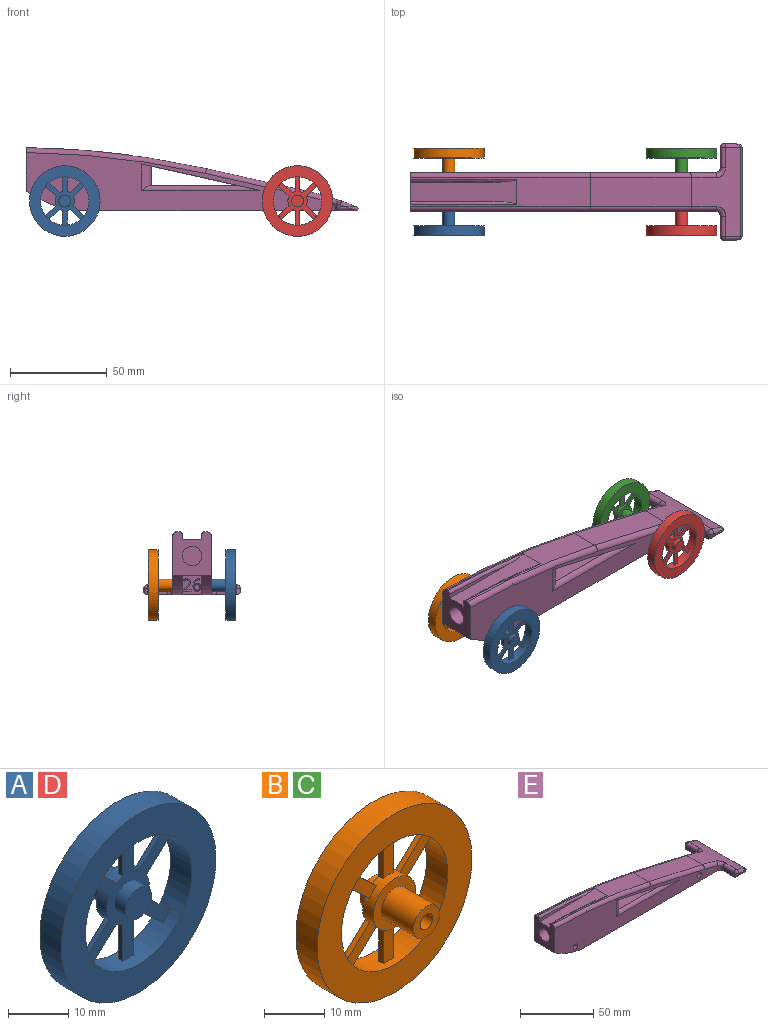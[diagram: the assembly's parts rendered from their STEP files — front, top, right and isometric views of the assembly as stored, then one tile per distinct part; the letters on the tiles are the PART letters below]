
ASSEMBLY  parts=5 mates=4
PART A: 31 faces, bbox 36.4x12.5x36.4 mm
  f0: cylinder r=3.1mm len=7.5mm, axis (0,1,0), area 146.1mm2, adj f2,f5
  f1: cylinder r=1.5mm len=10mm, axis (0,1,0), area 94.2mm2, adj f2,f3
  f2: plane 6.2x6.2mm, normal (0,1,0), area 23.1mm2, adj f0,f1
  f3: plane 3x3mm, normal (0,1,0), area 7.1mm2, adj f1
  f4: cylinder r=5mm len=10mm, axis (0,-1,0), area 64mm2, adj f5,f6,f9,f10,f11,f12,f13,f14
  f5: plane 10x10mm, normal (0,1,0), area 48.3mm2, adj f0,f4
  f6: plane 25.02x19.87mm, normal (0,-1,0), area 156.8mm2, adj f4,f8,f9,f10,f12,f13,f15,f16
  f7: plane 6.18x6.18mm, normal (0,-1,0), area 30mm2, adj f8
  f8: cylinder r=3.09mm len=6.18mm, axis (0,1,0), area 48.5mm2, adj f6,f7
  f9: plane 5.55x5.17mm, normal (0.68,0,-0.73), area 7.6mm2, adj f4,f6,f11,f27
  f10: plane 5.55x5.17mm, normal (-0.68,0,0.73), area 7.6mm2, adj f4,f6,f11,f27
  f11: plane 7.19x6.93mm, normal (0,1,0), area 18.1mm2, adj f4,f9,f10,f27
  f12: plane 7.59x1mm, normal (1,0,0), area 7.6mm2, adj f4,f6,f14,f27
  f13: plane 7.59x1mm, normal (-1,0,0), area 7.6mm2, adj f4,f6,f14,f27
  f14: plane 7.65x2.4mm, normal (0,1,0), area 18.1mm2, adj f4,f12,f13,f27
  f15: plane 5.55x5.17mm, normal (-0.68,0,-0.73), area 7.6mm2, adj f4,f6,f17,f27
  f16: plane 5.55x5.17mm, normal (0.68,0,0.73), area 7.6mm2, adj f4,f6,f17,f27
  f17: plane 7.19x6.93mm, normal (0,1,0), area 18.1mm2, adj f4,f15,f16,f27
  f18: plane 5.55x5.17mm, normal (-0.68,0,0.73), area 7.6mm2, adj f4,f6,f20,f27
  f19: plane 5.55x5.17mm, normal (0.68,0,-0.73), area 7.6mm2, adj f4,f6,f20,f27
  f20: plane 7.19x6.93mm, normal (0,1,0), area 18.1mm2, adj f4,f18,f19,f27
  f21: plane 7.59x1mm, normal (-1,0,0), area 7.6mm2, adj f4,f6,f23,f27
  f22: plane 7.59x1mm, normal (1,0,0), area 7.6mm2, adj f4,f6,f23,f27
  f23: plane 7.65x2.4mm, normal (0,1,0), area 18.1mm2, adj f4,f21,f22,f27
  f24: plane 5.55x5.17mm, normal (-0.68,0,-0.73), area 7.6mm2, adj f4,f6,f26,f27
  f25: plane 5.55x5.17mm, normal (0.68,0,0.73), area 7.6mm2, adj f4,f6,f26,f27
  f26: plane 7.19x6.93mm, normal (0,1,0), area 18.1mm2, adj f4,f24,f25,f27
  f27: cylinder r=12.5mm len=25mm, axis (0,1,0), area 378.3mm2, adj f6,f9,f10,f11,f12,f13,f14,f15
  f28: cylinder r=18.2mm len=36.4mm, axis (0,1,0), area 571.8mm2, adj f29,f30
  f29: plane 36.4x36.4mm, normal (0,-1,0), area 549.7mm2, adj f27,f28
  f30: plane 36.4x36.4mm, normal (0,1,0), area 549.7mm2, adj f27,f28
PART B: 31 faces, bbox 36.4x12.5x36.4 mm
  f0: cylinder r=3.1mm len=7.5mm, axis (0,-1,0), area 146.1mm2, adj f2,f5
  f1: cylinder r=1.5mm len=10mm, axis (0,-1,0), area 94.2mm2, adj f2,f3
  f2: plane 6.2x6.2mm, normal (0,-1,0), area 23.1mm2, adj f0,f1
  f3: plane 3x3mm, normal (0,-1,0), area 7.1mm2, adj f1
  f4: cylinder r=5mm len=10mm, axis (0,1,0), area 64mm2, adj f5,f6,f9,f10,f11,f12,f13,f14
  f5: plane 10x10mm, normal (0,-1,0), area 48.3mm2, adj f0,f4
  f6: plane 25.02x19.87mm, normal (0,1,0), area 156.8mm2, adj f4,f8,f9,f10,f12,f13,f15,f16
  f7: plane 6.18x6.18mm, normal (0,1,0), area 30mm2, adj f8
  f8: cylinder r=3.09mm len=6.18mm, axis (0,-1,0), area 48.5mm2, adj f6,f7
  f9: plane 5.55x5.17mm, normal (0.68,0,-0.73), area 7.6mm2, adj f4,f6,f11,f27
  f10: plane 5.55x5.17mm, normal (-0.68,0,0.73), area 7.6mm2, adj f4,f6,f11,f27
  f11: plane 7.19x6.93mm, normal (0,-1,0), area 18.1mm2, adj f4,f9,f10,f27
  f12: plane 7.59x1mm, normal (1,0,0), area 7.6mm2, adj f4,f6,f14,f27
  f13: plane 7.59x1mm, normal (-1,0,0), area 7.6mm2, adj f4,f6,f14,f27
  f14: plane 7.65x2.4mm, normal (0,-1,0), area 18.1mm2, adj f4,f12,f13,f27
  f15: plane 5.55x5.17mm, normal (-0.68,0,-0.73), area 7.6mm2, adj f4,f6,f17,f27
  f16: plane 5.55x5.17mm, normal (0.68,0,0.73), area 7.6mm2, adj f4,f6,f17,f27
  f17: plane 7.19x6.93mm, normal (0,-1,0), area 18.1mm2, adj f4,f15,f16,f27
  f18: plane 5.55x5.17mm, normal (-0.68,0,0.73), area 7.6mm2, adj f4,f6,f20,f27
  f19: plane 5.55x5.17mm, normal (0.68,0,-0.73), area 7.6mm2, adj f4,f6,f20,f27
  f20: plane 7.19x6.93mm, normal (0,-1,0), area 18.1mm2, adj f4,f18,f19,f27
  f21: plane 7.59x1mm, normal (-1,0,0), area 7.6mm2, adj f4,f6,f23,f27
  f22: plane 7.59x1mm, normal (1,0,0), area 7.6mm2, adj f4,f6,f23,f27
  f23: plane 7.65x2.4mm, normal (0,-1,0), area 18.1mm2, adj f4,f21,f22,f27
  f24: plane 5.55x5.17mm, normal (-0.68,0,-0.73), area 7.6mm2, adj f4,f6,f26,f27
  f25: plane 5.55x5.17mm, normal (0.68,0,0.73), area 7.6mm2, adj f4,f6,f26,f27
  f26: plane 7.19x6.93mm, normal (0,-1,0), area 18.1mm2, adj f4,f24,f25,f27
  f27: cylinder r=12.5mm len=25mm, axis (0,-1,0), area 378.3mm2, adj f6,f9,f10,f11,f12,f13,f14,f15
  f28: cylinder r=18.2mm len=36.4mm, axis (0,-1,0), area 571.8mm2, adj f29,f30
  f29: plane 36.4x36.4mm, normal (0,1,0), area 549.7mm2, adj f27,f28
  f30: plane 36.4x36.4mm, normal (0,-1,0), area 549.7mm2, adj f27,f28
PART C: same geometry as B
PART D: same geometry as A
PART E: 107 faces, bbox 179.9x56.5x40.9 mm
  f0: plane 10x10mm, normal (-1,0,0), area 75.3mm2, adj f4,f35,f36,f37,f59,f60,f61,f62
  f1: cylinder r=450mm len=93.08mm, axis (0,-1,0), area 694mm2, adj f6,f8,f38,f44,f56,f57,f58
  f2: cylinder r=2.29mm len=5mm, axis (0,-1,0), area 71.9mm2, adj f5,f35
  f3: plane 5.97x5mm, normal (-0.5,0,-0.87), area 34.4mm2, adj f5,f6,f35,f53
  f4: plane 139.38x46mm, normal (0,0,-1), area 2062.3mm2, adj f0,f5,f7,f18,f20,f22,f25,f34
  f5: plane 157.5x30mm, normal (0,1,0), area 2648.8mm2, adj f2,f3,f4,f6,f10,f16,f38,f39
  f6: plane 22.51x20.01mm, normal (-1,0,0), area 327.8mm2, adj f1,f3,f5,f7,f12,f17,f37,f38
  f7: plane 157.5x30mm, normal (0,-1,0), area 2648.8mm2, adj f4,f6,f10,f11,f16,f17,f43,f44
  f8: plane 51.92x15mm, normal (0.22,0,0.98), area 798.1mm2, adj f1,f9,f40,f46
  f9: cylinder r=156.42mm len=46mm, axis (0,-1,0), area 687.1mm2, adj f8,f22,f23,f28,f29,f31,f41,f42
  f10: cylinder r=2.29mm len=20mm, axis (0,-1,0), area 287.5mm2, adj f5,f7
  f11: cylinder r=2.29mm len=5mm, axis (0,-1,0), area 71.9mm2, adj f7,f36
  f12: cylinder r=5mm len=60mm, axis (-1,0,0), area 1885mm2, adj f6,f13
  f13: plane 10x10mm, normal (-1,0,0), area 78.5mm2, adj f12
  f14: plane 10.02x10mm, normal (1,0,0), area 100.2mm2, adj f15,f16,f48,f49
  f15: plane 45.33x15mm, normal (0,0,1), area 671mm2, adj f14,f16,f48,f49,f50,f51
  f16: plane 65.54x24.69mm, normal (-0.22,0,-0.98), area 939.3mm2, adj f5,f7,f14,f15,f48,f49,f50,f51
  f17: plane 5.97x5mm, normal (-0.5,0,-0.87), area 34.4mm2, adj f6,f7,f36,f52
  f18: plane 10.5x3.05mm, normal (-1,0,0), area 32mm2, adj f4,f29,f32,f43
  f19: plane 2.89x1.05mm, normal (0,-1,0), area 1.5mm2, adj f31,f32,f34
  f20: plane 10.5x3.05mm, normal (-1,0,0), area 32mm2, adj f4,f23,f24,f39
  f21: plane 2.89x1.05mm, normal (0,1,0), area 1.5mm2, adj f24,f25,f28
  f22: cylinder r=1mm len=46mm, axis (0,-1,0), area 126.5mm2, adj f4,f9,f27,f33
  f23: cylinder r=2mm len=10.5mm, axis (0,-1,0), area 40.1mm2, adj f9,f20,f26,f41
  f24: cylinder r=2mm len=3.05mm, axis (0,0,-1), area 6.4mm2, adj f20,f21,f25,f26
  f25: cylinder r=2mm len=10.16mm, axis (-1,0,0), area 20.5mm2, adj f4,f21,f24,f27
  f26: sphere r=2mm, area 7.8mm2, adj f23,f24,f28
  f27: bspline ~10.31x3.14mm, area 7.1mm2, adj f22,f25,f28
  f28: torus R=154.42mm, axis (0,1,0), area 18.1mm2, adj f9,f21,f26,f27
  f29: cylinder r=2mm len=10.5mm, axis (0,-1,0), area 40.1mm2, adj f9,f18,f30,f45
  f30: sphere r=2mm, area 7.5mm2, adj f29,f31,f32
  f31: torus R=154.42mm, axis (0,-1,0), area 18.1mm2, adj f9,f19,f30,f33
  f32: cylinder r=2mm len=3.05mm, axis (0,0,1), area 6.4mm2, adj f18,f19,f30,f34
  f33: bspline ~10.31x3.79mm, area 7.1mm2, adj f22,f31,f34
  f34: cylinder r=2mm len=10.16mm, axis (-1,0,0), area 20.5mm2, adj f4,f19,f32,f33
  f35: plane 130x10mm, normal (0,-1,0), area 1181.1mm2, adj f0,f2,f3,f4,f37,f53
  f36: plane 130x10mm, normal (0,1,0), area 1181.1mm2, adj f0,f4,f11,f17,f37,f52
  f37: plane 130x10mm, normal (0,0,-1), area 1300mm2, adj f0,f6,f35,f36
  f38: torus R=447.5mm, axis (0,1,0), area 367.9mm2, adj f1,f5,f6,f40
  f39: cylinder r=2.5mm len=4.03mm, axis (0,0,1), area 13.9mm2, adj f4,f5,f20,f41
  f40: cylinder r=2.5mm len=52.47mm, axis (0.98,0,-0.22), area 208.9mm2, adj f5,f8,f38,f42
  f41: bspline ~5.16x5mm, area 20.6mm2, adj f9,f23,f39,f42
  f42: torus R=153.92mm, axis (0,1,0), area 53.6mm2, adj f5,f9,f40,f41
  f43: cylinder r=2.5mm len=4.03mm, axis (0,0,1), area 13.9mm2, adj f4,f7,f18,f45
  f44: torus R=447.5mm, axis (0,1,0), area 367.9mm2, adj f1,f6,f7,f46
  f45: bspline ~5.16x5mm, area 20.6mm2, adj f9,f29,f43,f47
  f46: cylinder r=2.5mm len=52.47mm, axis (0.98,0,-0.22), area 208.9mm2, adj f7,f8,f44,f47
  f47: torus R=153.92mm, axis (0,1,0), area 53.6mm2, adj f7,f9,f45,f46
  f48: cylinder r=5mm len=13.66mm, axis (0,0,-1), area 89.6mm2, adj f5,f14,f15,f16,f50
  f49: cylinder r=5mm len=13.66mm, axis (0,0,-1), area 89.6mm2, adj f7,f14,f15,f16,f51
  f50: cylinder r=2.5mm len=60.81mm, axis (1,0,0), area 208.4mm2, adj f5,f15,f16,f48
  f51: cylinder r=2.5mm len=60.81mm, axis (1,0,0), area 208.4mm2, adj f7,f15,f16,f49
  f52: cylinder r=50mm len=24.81mm, axis (0,1,0), area 129.8mm2, adj f4,f7,f17,f36
  f53: cylinder r=50mm len=24.81mm, axis (0,1,0), area 129.8mm2, adj f3,f4,f5,f35
  f54: plane 42.25x2.5mm, normal (0,1,0), area 66.9mm2, adj f6,f56,f57
  f55: plane 42.25x2.5mm, normal (0,-1,0), area 66.9mm2, adj f6,f56,f58
  f56: plane 55.85x14.08mm, normal (0,0,1), area 555.2mm2, adj f1,f6,f54,f55,f57,f58
  f57: torus R=448.5mm, axis (0,1,0), area 114.6mm2, adj f1,f6,f54,f56
  f58: torus R=448.5mm, axis (0,1,0), area 114.6mm2, adj f1,f6,f55,f56
  f59: extruded ~2.03x0.57mm, area 0.4mm2, adj f0,f60,f83,f84
  f60: extruded ~1.54x0.73mm, area 0.4mm2, adj f0,f59,f61,f84
  f61: extruded ~1.44x0.56mm, area 0.3mm2, adj f0,f60,f62,f84
  f62: extruded ~1.53x0.53mm, area 0.3mm2, adj f0,f61,f63,f84
  f63: extruded ~1.38x0.49mm, area 0.3mm2, adj f0,f62,f64,f84
  f64: extruded ~1.33x0.51mm, area 0.3mm2, adj f0,f63,f65,f84
  f65: extruded ~1.49x0.74mm, area 0.3mm2, adj f0,f64,f66,f84
  f66: plane 0.2x0.05mm, normal (0,0,-1), area 0mm2, adj f0,f65,f67,f84
  f67: extruded ~1.97x0.58mm, area 0.4mm2, adj f0,f66,f68,f84
  f68: extruded ~1.54x0.63mm, area 0.3mm2, adj f0,f67,f69,f84
  f69: extruded ~0.75x0.2mm, area 0.2mm2, adj f0,f68,f70,f84
  f70: plane 0.61x0.2mm, normal (0,1,0), area 0.1mm2, adj f0,f69,f71,f84
  f71: extruded ~0.76x0.2mm, area 0.2mm2, adj f0,f70,f72,f84
  f72: extruded ~2.12x0.91mm, area 0.5mm2, adj f0,f71,f83,f84
  f73: extruded ~0.72x0.22mm, area 0.2mm2, adj f74,f82,f84,f85
  f74: extruded ~0.6x0.49mm, area 0.2mm2, adj f73,f75,f84,f85
  f75: extruded ~0.82x0.2mm, area 0.2mm2, adj f74,f76,f84,f85
  f76: extruded ~0.58x0.2mm, area 0.1mm2, adj f75,f77,f84,f85
  f77: extruded ~0.51x0.44mm, area 0.1mm2, adj f76,f78,f84,f85
  f78: extruded ~0.71x0.2mm, area 0.1mm2, adj f77,f79,f84,f85
  f79: extruded ~0.93x0.36mm, area 0.2mm2, adj f78,f80,f84,f85
  f80: extruded ~0.97x0.31mm, area 0.2mm2, adj f79,f81,f84,f85
  f81: extruded ~1.11x0.34mm, area 0.2mm2, adj f80,f82,f84,f85
  f82: extruded ~0.94x0.38mm, area 0.2mm2, adj f73,f81,f84,f85
  f83: extruded ~2.76x0.72mm, area 0.6mm2, adj f0,f59,f72,f84
  f84: plane 6.43x4.08mm, normal (-1,0,0), area 10.1mm2, adj f59,f60,f61,f62,f63,f64,f65,f66
  f85: plane 2.82x2.65mm, normal (-1,0,0), area 6mm2, adj f73,f74,f75,f76,f77,f78,f79,f80
  f86: plane 0.66x0.2mm, normal (0,1,0), area 0.1mm2, adj f0,f87,f105,f106
  f87: plane 3.21x0.2mm, normal (0,0,-1), area 0.6mm2, adj f0,f86,f88,f106
  f88: plane 0.2x0.03mm, normal (0,1,0), area 0mm2, adj f0,f87,f89,f106
  f89: plane 1.37x1.34mm, normal (0,0.7,0.71), area 0.4mm2, adj f0,f88,f90,f106
  f90: extruded ~1.47x1.25mm, area 0.4mm2, adj f0,f89,f91,f106
  f91: extruded ~1.18x0.33mm, area 0.2mm2, adj f0,f90,f92,f106
  f92: extruded ~1.21x0.5mm, area 0.3mm2, adj f0,f91,f93,f106
  f93: extruded ~1.38x0.45mm, area 0.3mm2, adj f0,f92,f94,f106
  f94: extruded ~1.88x0.72mm, area 0.4mm2, adj f0,f93,f95,f106
  f95: plane 0.48x0.38mm, normal (0,-0.79,0.61), area 0.1mm2, adj f0,f94,f96,f106
  f96: extruded ~0.78x0.47mm, area 0.2mm2, adj f0,f95,f97,f106
  f97: extruded ~0.74x0.2mm, area 0.2mm2, adj f0,f96,f98,f106
  f98: extruded ~0.84x0.29mm, area 0.2mm2, adj f0,f97,f99,f106
  f99: extruded ~0.79x0.3mm, area 0.2mm2, adj f0,f98,f100,f106
  f100: extruded ~0.66x0.2mm, area 0.1mm2, adj f0,f99,f101,f106
  f101: extruded ~0.63x0.36mm, area 0.1mm2, adj f0,f100,f102,f106
  f102: extruded ~1.09x0.99mm, area 0.3mm2, adj f0,f101,f103,f106
  f103: plane 1.65x1.65mm, normal (0,-0.71,-0.71), area 0.5mm2, adj f0,f102,f104,f106
  f104: plane 0.61x0.2mm, normal (0,-1,0), area 0.1mm2, adj f0,f103,f105,f106
  f105: plane 4.11x0.2mm, normal (0,0,1), area 0.8mm2, adj f0,f86,f104,f106
  f106: plane 6.34x4.11mm, normal (-1,0,0), area 8.6mm2, adj f86,f87,f88,f89,f90,f91,f92,f93
PLACE A t=(-89.77,-26.52,3.02)mm
PLACE B t=(-89.77,-31.52,3.02)mm
PLACE C t=(30.23,-31.52,3.02)mm
PLACE D t=(30.23,-26.52,3.02)mm
PLACE E t=(-29.71,-3.26,-1.98)mm
MATE revolute A.f0 <-> E.f2  axis (0,1,0) through (-89.77,-26.52,3.02)mm
MATE revolute D.f1 <-> E.f10  axis (0,1,0) through (30.23,-26.52,3.02)mm
MATE revolute C.f1 <-> E.f10  axis (0,-1,0) through (30.23,-6.52,3.02)mm
MATE revolute B.f1 <-> E.f2  axis (0,-1,0) through (-89.77,-6.52,3.02)mm
